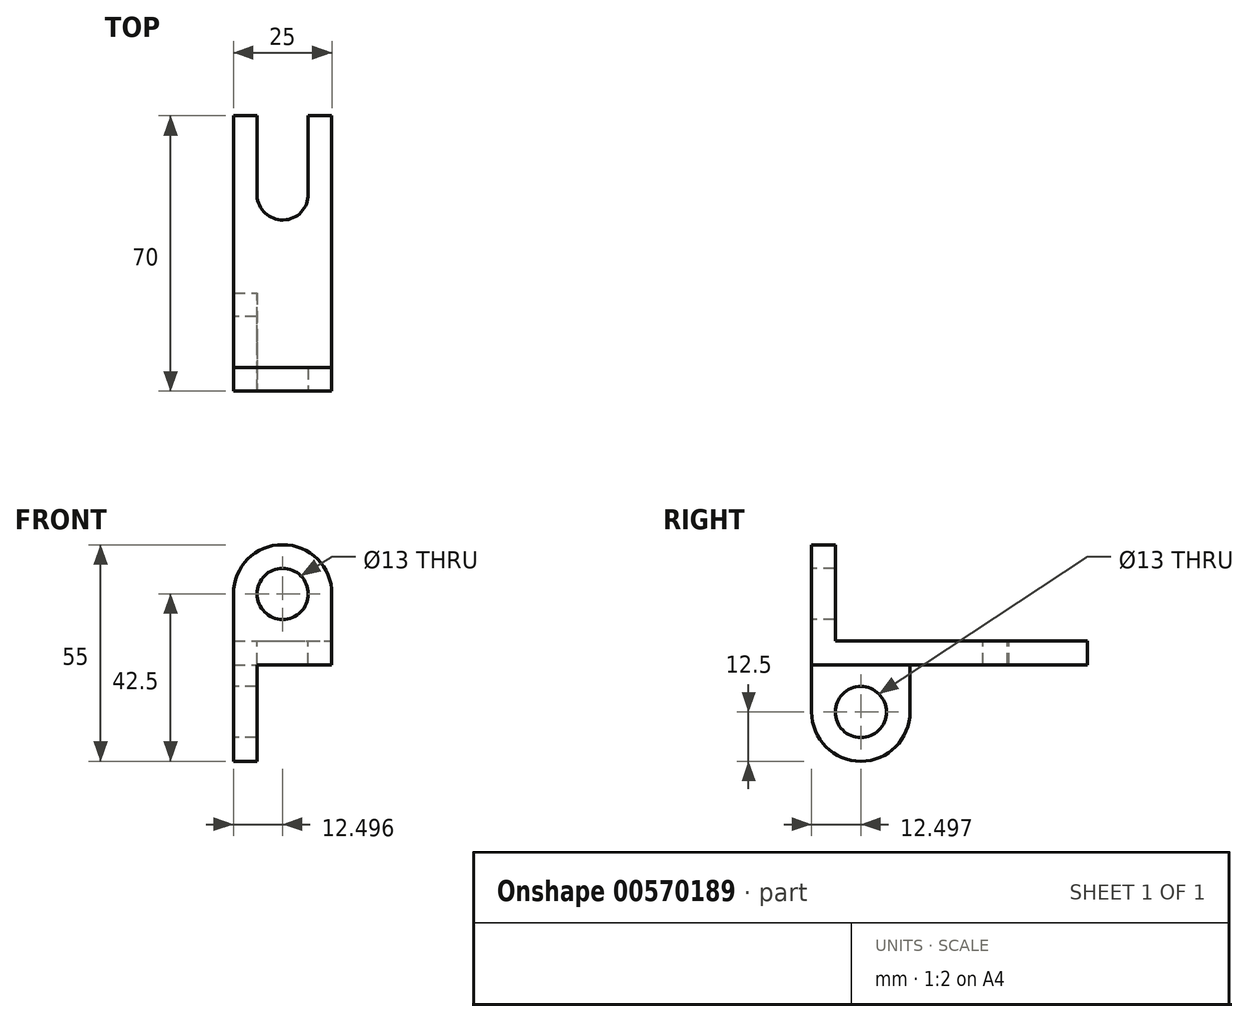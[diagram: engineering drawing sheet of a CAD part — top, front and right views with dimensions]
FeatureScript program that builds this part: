
annotation { "Feature Type Name" : "Feature", "Feature Type Description" : "" }
export const myFeature = defineFeature(function(context is Context, id is Id, definition is map)
    precondition{}
    {
        {
            var Q0;
            Q0=qCreatedBy(makeId("Top.planeOp"),FACE);
            var sketch = newSketch(context, id + "F0", { "sketchPlane" : qUnion([Q0])});
            skLineSegment(sketch, "E0.bottom", {"start": v(-14.8, -31.04) * mm, "end": v(10.2, -31.04) * mm});
            skLineSegment(sketch, "E0.top", {"start": v(-14.8, 38.96) * mm, "end": v(10.2, 38.96) * mm});
            skLineSegment(sketch, "E0.left", {"start": v(-14.8, -31.04) * mm, "end": v(-14.8, 38.96) * mm});
            skLineSegment(sketch, "E0.right", {"start": v(10.2, -31.04) * mm, "end": v(10.2, 38.96) * mm});
            skSolve(sketch);
        }
        {
            var Q0;
            Q0 = qSketchRegion(id + "F0", true);
            extrude(context, id + "F1", {"entities" : qUnion([Q0]), "depth" : 6 * mm, "offsetDistance" : 25 * mm});
        }
        {
            var Q0;
            Q0=makeQuery(id+"F1.opExtrude","CAP_FACE",FACE,{"disambiguationData":[OSD([sQuery(id+"F0.wireOp",EDGE,"E0.bottom"),sQuery(id+"F0.wireOp",EDGE,"E0.top"),sQuery(id+"F0.wireOp",EDGE,"E0.left"),sQuery(id+"F0.wireOp",EDGE,"E0.right")])],"isStart":false});
            var sketch = newSketch(context, id + "F2", { "sketchPlane" : qUnion([Q0])});
            skLineSegment(sketch, "E1.bottom", {"start": v(-14.8, -31.04) * mm, "end": v(10.2, -31.04) * mm});
            skLineSegment(sketch, "E1.top", {"start": v(-14.8, -25.04) * mm, "end": v(10.2, -25.04) * mm});
            skLineSegment(sketch, "E1.left", {"start": v(-14.8, -31.04) * mm, "end": v(-14.8, -25.04) * mm});
            skLineSegment(sketch, "E1.right", {"start": v(10.2, -31.04) * mm, "end": v(10.2, -25.04) * mm});
            skSolve(sketch);
        }
        {
            var Q0;
            Q0=makeQuery(id+"F2.imprint","IMPRINT",FACE,{"disambiguationData":[TD([[makeQuery(id+"F2.imprint","IMPRINT",EDGE,{"derivedFrom":sQuery(id+"F2.wireOp",EDGE,"E1.bottom")}),1.0]])]});
            extrude(context, id + "F3", {"entities" : qUnion([Q0]), "operationType" : NewBodyOperationType.ADD, "depth" : 12 * mm, "offsetDistance" : 25 * mm});
        }
        {
            var Q0;
            Q0=makeQuery(id+"F3.boolean.opBoolean","MERGE",FACE,{"derivedFrom":[makeQuery(id+"F1.opExtrude","SWEPT_FACE",FACE,{"disambiguationData":[OSD([sQuery(id+"F0.wireOp",EDGE,"E0.bottom")])]}),makeQuery(id+"F3.opExtrude","SWEPT_FACE",FACE,{"disambiguationData":[OSD([sQuery(id+"F2.wireOp",EDGE,"E1.bottom")])]})]});
            var sketch = newSketch(context, id + "F4", { "sketchPlane" : qUnion([Q0])});
            skCircle(sketch, "E2", {"center": v(-2.3, 18) * mm, "radius": 12.5 * mm});
            skSolve(sketch);
        }
        {
            var Q0;
            {var subQ1=sQuery(id+"F2.wireOp",EDGE,"E1.bottom");var subQ3=makeQuery(id+"F3.opExtrude","CAP_EDGE",EDGE,{"disambiguationData":[OSD([subQ1])],"isStart":false});Q0=makeQuery(id+"F4.imprint","IMPRINT",FACE,{"disambiguationData":[TD([[makeQuery(id+"F4.imprint","IMPRINT",EDGE,{"derivedFrom":subQ3}),1.0]])]});}
            extrude(context, id + "F5", {"entities" : qUnion([Q0]), "operationType" : NewBodyOperationType.ADD, "oppositeDirection" : true, "depth" : 6 * mm, "offsetDistance" : 25 * mm});
        }
        {
            var Q0;
            {var subQ0=sQuery(id+"F2.wireOp",EDGE,"E1.bottom");Q0=makeQuery(id+"F5.boolean.opBoolean","MERGE",FACE,{"derivedFrom":[makeQuery(id+"F3.boolean.opBoolean","MERGE",FACE,{"derivedFrom":[makeQuery(id+"F1.opExtrude","SWEPT_FACE",FACE,{"disambiguationData":[OSD([sQuery(id+"F0.wireOp",EDGE,"E0.bottom")])]}),makeQuery(id+"F3.opExtrude","SWEPT_FACE",FACE,{"disambiguationData":[OSD([subQ0])]})]}),makeQuery(id+"F5.opExtrude","CAP_FACE",FACE,{"disambiguationData":[OSD([subQ0,sQuery(id+"F4.wireOp",EDGE,"E2")])],"isStart":true})]});}
            var sketch = newSketch(context, id + "F6", { "sketchPlane" : qUnion([Q0])});
            skCircle(sketch, "E3", {"center": v(-2.3, 18) * mm, "radius": 6.5 * mm});
            skSolve(sketch);
        }
        {
            var Q0;
            Q0=makeQuery(id+"F6.imprint","IMPRINT",FACE,{"disambiguationData":[TD([[makeQuery(id+"F6.imprint","IMPRINT",EDGE,{"derivedFrom":sQuery(id+"F6.wireOp",EDGE,"E3")}),1.0]])]});
            extrude(context, id + "F7", {"entities" : qUnion([Q0]), "operationType" : NewBodyOperationType.REMOVE, "oppositeDirection" : true, "depth" : 25 * mm, "offsetDistance" : 25 * mm});
        }
        {
            var Q0;
            Q0=makeQuery(id+"F1.opExtrude","CAP_FACE",FACE,{"disambiguationData":[OSD([sQuery(id+"F0.wireOp",EDGE,"E0.bottom"),sQuery(id+"F0.wireOp",EDGE,"E0.top"),sQuery(id+"F0.wireOp",EDGE,"E0.left"),sQuery(id+"F0.wireOp",EDGE,"E0.right")])],"isStart":false});
            var sketch = newSketch(context, id + "F8", { "sketchPlane" : qUnion([Q0])});
            skCircle(sketch, "E4", {"center": v(-2.3, 18.96) * mm, "radius": 6.5 * mm});
            skPoint(sketch, "E4.centerSnap0", {"position": v(-2.3, 38.96) * mm});
            skLineSegment(sketch, "E5", {"start": v(4.2, 19.07) * mm, "end": v(4.2, 38.96) * mm});
            skLineSegment(sketch, "E6", {"start": v(-8.79, 18.72) * mm, "end": v(-8.79, 38.96) * mm});
            skSolve(sketch);
        }
        {
            var Q0;
            {var subQ0=sQuery(id+"F8.wireOp",EDGE,"E4");var subQ1=makeQuery(id+"F8.imprint","INTERSECT",VERTEX,{"derivedFrom":[subQ0,sQuery(id+"F8.wireOp",EDGE,"E5")]});Q0=makeQuery(id+"F8.imprint","IMPRINT",FACE,{"disambiguationData":[TD([[makeQuery(id+"F8.imprint","IMPRINT",EDGE,{"disambiguationData":[TD([[subQ1,-1.0]])],"derivedFrom":subQ0}),1.0]])]});}
            var Q1;
            {var subQ0=sQuery(id+"F8.wireOp",EDGE,"E5");Q1=makeQuery(id+"F8.imprint","IMPRINT",FACE,{"disambiguationData":[TD([[makeQuery(id+"F8.imprint","IMPRINT",EDGE,{"derivedFrom":subQ0}),1.0]])]});}
            extrude(context, id + "F9", {"entities" : qUnion([Q0, Q1]), "operationType" : NewBodyOperationType.REMOVE, "oppositeDirection" : true, "depth" : 25 * mm, "offsetDistance" : 25 * mm});
        }
        {
            var Q0;
            Q0=makeQuery(id+"F1.opExtrude","CAP_FACE",FACE,{"disambiguationData":[OSD([sQuery(id+"F0.wireOp",EDGE,"E0.bottom"),sQuery(id+"F0.wireOp",EDGE,"E0.top"),sQuery(id+"F0.wireOp",EDGE,"E0.left"),sQuery(id+"F0.wireOp",EDGE,"E0.right")])],"isStart":true});
            var sketch = newSketch(context, id + "F10", { "sketchPlane" : qUnion([Q0])});
            skLineSegment(sketch, "E7.bottom", {"start": v(-14.8, 31.04) * mm, "end": v(-8.8, 31.04) * mm});
            skLineSegment(sketch, "E7.top", {"start": v(-14.8, 6.04) * mm, "end": v(-8.8, 6.04) * mm});
            skLineSegment(sketch, "E7.left", {"start": v(-14.8, 31.04) * mm, "end": v(-14.8, 6.04) * mm});
            skLineSegment(sketch, "E7.right", {"start": v(-8.8, 31.04) * mm, "end": v(-8.8, 6.04) * mm});
            skSolve(sketch);
        }
        {
            var Q0;
            Q0=makeQuery(id+"F10.imprint","IMPRINT",FACE,{"disambiguationData":[TD([[makeQuery(id+"F10.imprint","IMPRINT",EDGE,{"derivedFrom":sQuery(id+"F10.wireOp",EDGE,"E7.bottom")}),-1.0]])]});
            extrude(context, id + "F11", {"entities" : qUnion([Q0]), "operationType" : NewBodyOperationType.ADD, "depth" : 12 * mm, "offsetDistance" : 25 * mm});
        }
        {
            var Q0;
            Q0=makeQuery(id+"F11.boolean.opBoolean","MERGE",FACE,{"derivedFrom":[makeQuery(id+"F3.boolean.opBoolean","MERGE",FACE,{"derivedFrom":[makeQuery(id+"F1.opExtrude","SWEPT_FACE",FACE,{"disambiguationData":[OSD([sQuery(id+"F0.wireOp",EDGE,"E0.left")])]}),makeQuery(id+"F3.opExtrude","SWEPT_FACE",FACE,{"disambiguationData":[OSD([sQuery(id+"F2.wireOp",EDGE,"E1.left")])]})]}),makeQuery(id+"F11.opExtrude","SWEPT_FACE",FACE,{"disambiguationData":[OSD([sQuery(id+"F10.wireOp",EDGE,"E7.left")])]})]});
            var sketch = newSketch(context, id + "F12", { "sketchPlane" : qUnion([Q0])});
            skCircle(sketch, "E8", {"center": v(18.54, -12) * mm, "radius": 12.5 * mm});
            skSolve(sketch);
        }
        {
            var Q0;
            {var subQ1=sQuery(id+"F10.wireOp",EDGE,"E7.left");var subQ3=makeQuery(id+"F11.opExtrude","CAP_EDGE",EDGE,{"disambiguationData":[OSD([subQ1])],"isStart":false});Q0=makeQuery(id+"F12.imprint","IMPRINT",FACE,{"disambiguationData":[TD([[makeQuery(id+"F12.imprint","IMPRINT",EDGE,{"derivedFrom":subQ3}),1.0]])]});}
            extrude(context, id + "F13", {"entities" : qUnion([Q0]), "operationType" : NewBodyOperationType.ADD, "oppositeDirection" : true, "depth" : 6 * mm, "offsetDistance" : 25 * mm});
        }
        {
            var Q0;
            {var subQ0=sQuery(id+"F10.wireOp",EDGE,"E7.left");Q0=makeQuery(id+"F13.boolean.opBoolean","MERGE",FACE,{"derivedFrom":[makeQuery(id+"F11.boolean.opBoolean","MERGE",FACE,{"derivedFrom":[makeQuery(id+"F3.boolean.opBoolean","MERGE",FACE,{"derivedFrom":[makeQuery(id+"F1.opExtrude","SWEPT_FACE",FACE,{"disambiguationData":[OSD([sQuery(id+"F0.wireOp",EDGE,"E0.left")])]}),makeQuery(id+"F3.opExtrude","SWEPT_FACE",FACE,{"disambiguationData":[OSD([sQuery(id+"F2.wireOp",EDGE,"E1.left")])]})]}),makeQuery(id+"F11.opExtrude","SWEPT_FACE",FACE,{"disambiguationData":[OSD([subQ0])]})]}),makeQuery(id+"F13.opExtrude","CAP_FACE",FACE,{"disambiguationData":[OSD([subQ0,sQuery(id+"F12.wireOp",EDGE,"E8")])],"isStart":true})]});}
            var sketch = newSketch(context, id + "F14", { "sketchPlane" : qUnion([Q0])});
            skCircle(sketch, "E9", {"center": v(18.54, -12) * mm, "radius": 6.5 * mm});
            skSolve(sketch);
        }
        {
            var Q0;
            Q0=makeQuery(id+"F14.imprint","IMPRINT",FACE,{"disambiguationData":[TD([[makeQuery(id+"F14.imprint","IMPRINT",EDGE,{"derivedFrom":sQuery(id+"F14.wireOp",EDGE,"E9")}),1.0]])]});
            extrude(context, id + "F15", {"entities" : qUnion([Q0]), "operationType" : NewBodyOperationType.REMOVE, "oppositeDirection" : true, "depth" : 25 * mm, "offsetDistance" : 25 * mm});
        }
    });
